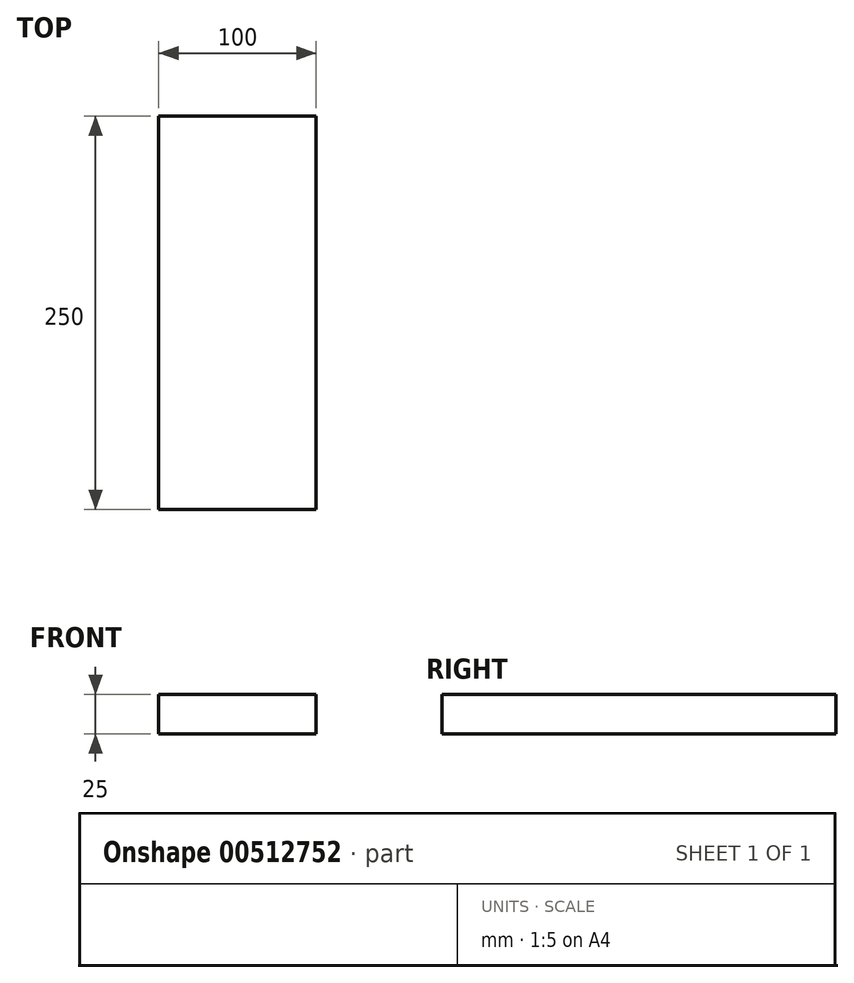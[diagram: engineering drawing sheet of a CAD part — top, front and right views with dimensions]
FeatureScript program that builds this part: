
annotation { "Feature Type Name" : "Feature", "Feature Type Description" : "" }
export const myFeature = defineFeature(function(context is Context, id is Id, definition is map)
    precondition{}
    {
        {
            var Q0;
            Q0=qCreatedBy(makeId("Top.planeOp"),FACE);
            var sketch = newSketch(context, id + "F0", { "sketchPlane" : qUnion([Q0])});
            skLineSegment(sketch, "E0.bottom", {"start": v(50, -125) * mm, "end": v(-50, -125) * mm});
            skLineSegment(sketch, "E0.top", {"start": v(50, 125) * mm, "end": v(-50, 125) * mm});
            skLineSegment(sketch, "E0.left", {"start": v(50, -125) * mm, "end": v(50, 125) * mm});
            skLineSegment(sketch, "E0.right", {"start": v(-50, -125) * mm, "end": v(-50, 125) * mm});
            skPoint(sketch, "E0.middle", {"position": v(0, 0) * mm});
            skSolve(sketch);
        }
        {
            var Q0;
            Q0 = qSketchRegion(id + "F0", true);
            extrude(context, id + "F1", {"entities" : qUnion([Q0]), "depth" : 25 * mm, "offsetDistance" : 25 * mm});
        }
    });
